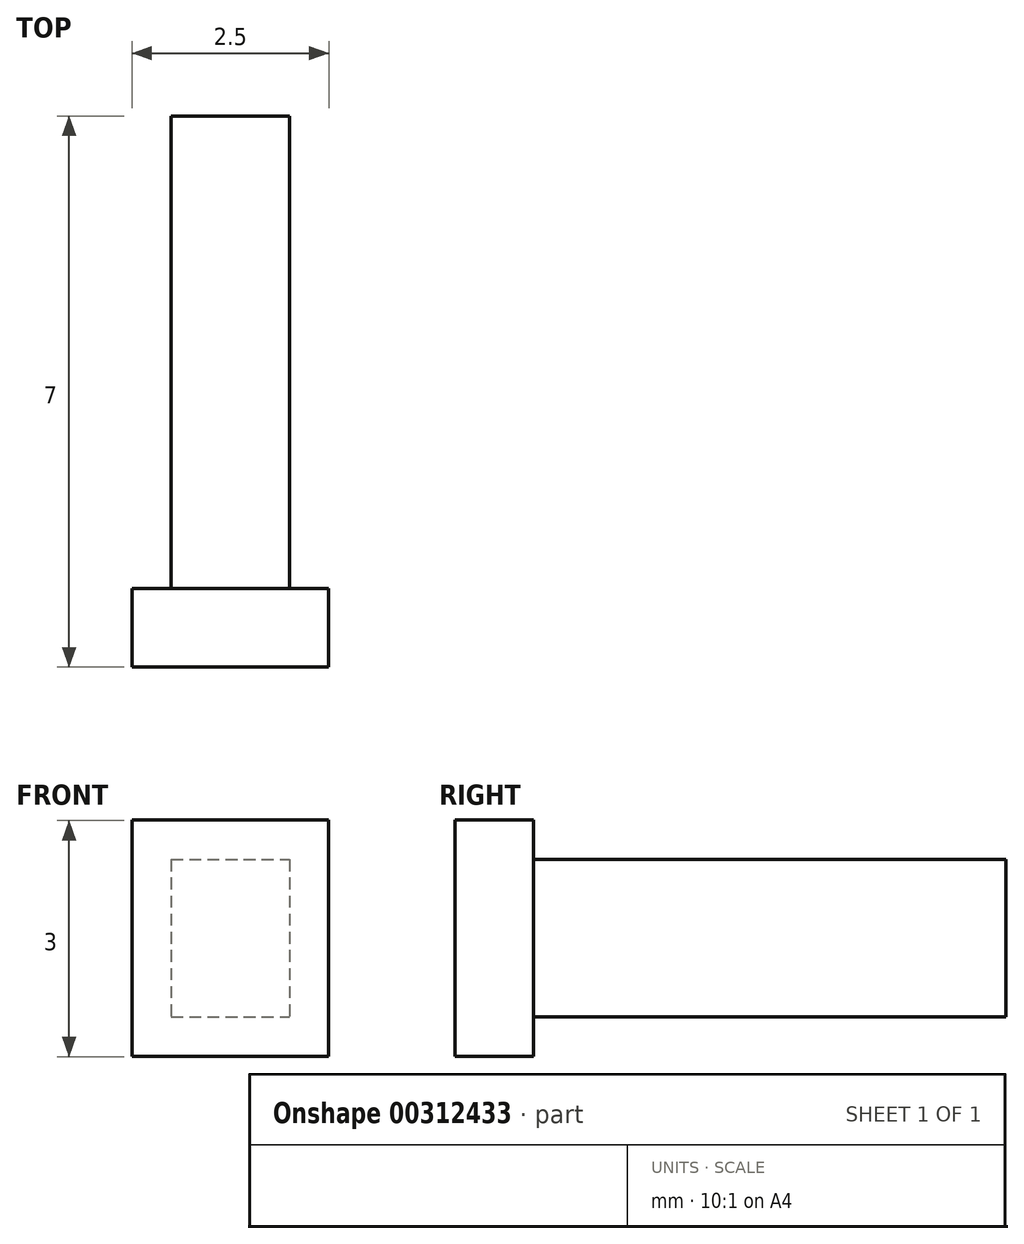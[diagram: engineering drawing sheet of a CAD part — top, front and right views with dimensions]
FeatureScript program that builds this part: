
annotation { "Feature Type Name" : "Feature", "Feature Type Description" : "" }
export const myFeature = defineFeature(function(context is Context, id is Id, definition is map)
    precondition{}
    {
        {
            var Q0;
            Q0=qCreatedBy(makeId("Front.planeOp"),FACE);
            var sketch = newSketch(context, id + "F0", { "sketchPlane" : qUnion([Q0])});
            skLineSegment(sketch, "E0.bottom", {"start": v(-0.36, -2.35) * mm, "end": v(1.14, -2.35) * mm});
            skLineSegment(sketch, "E0.top", {"start": v(-0.36, -4.35) * mm, "end": v(1.14, -4.35) * mm});
            skLineSegment(sketch, "E0.left", {"start": v(-0.36, -2.35) * mm, "end": v(-0.36, -4.35) * mm});
            skLineSegment(sketch, "E0.right", {"start": v(1.14, -2.35) * mm, "end": v(1.14, -4.35) * mm});
            skSolve(sketch);
        }
        {
            var Q0;
            Q0 = qSketchRegion(id + "F0", true);
            extrude(context, id + "F1", {"entities" : qUnion([Q0]), "depth" : 6 * mm});
        }
        {
            var Q0;
            Q0=makeQuery(id+"F1.opExtrude","CAP_FACE",FACE,{"disambiguationData":[OSD([sQuery(id+"F0.wireOp",EDGE,"E0.bottom"),sQuery(id+"F0.wireOp",EDGE,"E0.top"),sQuery(id+"F0.wireOp",EDGE,"E0.left"),sQuery(id+"F0.wireOp",EDGE,"E0.right")])],"isStart":false});
            var sketch = newSketch(context, id + "F2", { "sketchPlane" : qUnion([Q0])});
            skLineSegment(sketch, "E1.bottom", {"start": v(-0.86, -1.85) * mm, "end": v(1.64, -1.85) * mm});
            skLineSegment(sketch, "E1.top", {"start": v(-0.86, -4.85) * mm, "end": v(1.64, -4.85) * mm});
            skLineSegment(sketch, "E1.left", {"start": v(-0.86, -1.85) * mm, "end": v(-0.86, -4.85) * mm});
            skLineSegment(sketch, "E1.right", {"start": v(1.64, -1.85) * mm, "end": v(1.64, -4.85) * mm});
            skSolve(sketch);
        }
        {
            var Q0;
            Q0 = qSketchRegion(id + "F2", true);
            extrude(context, id + "F3", {"entities" : qUnion([Q0]), "operationType" : NewBodyOperationType.ADD, "depth" : 1 * mm});
        }
        {
            var Q0;
            Q0 = qSketchRegion(id + "F2", true);
            extrude(context, id + "F4", {"entities" : qUnion([Q0]), "operationType" : NewBodyOperationType.ADD, "depth" : 1 * mm});
        }
    });
